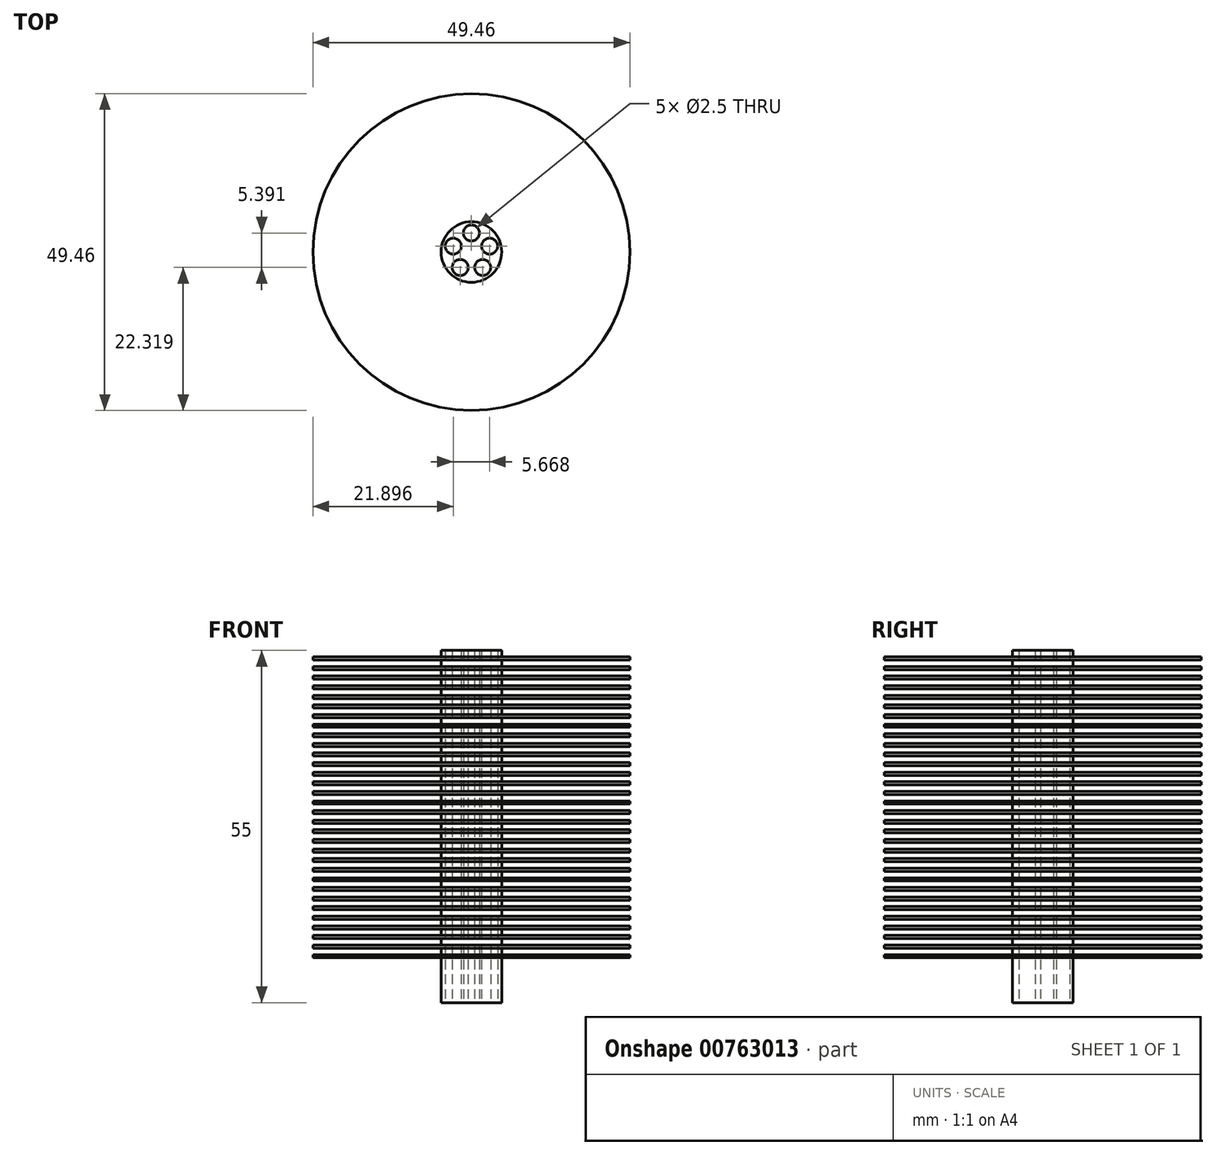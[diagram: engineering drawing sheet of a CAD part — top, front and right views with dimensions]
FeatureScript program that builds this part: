
annotation { "Feature Type Name" : "Feature", "Feature Type Description" : "" }
export const myFeature = defineFeature(function(context is Context, id is Id, definition is map)
    precondition{}
    {
        {
            var Q0;
            Q0=qCreatedBy(makeId("Top.planeOp"),FACE);
            var sketch = newSketch(context, id + "F0", { "sketchPlane" : qUnion([Q0])});
            skCircle(sketch, "E0", {"center": v(0, 0) * mm, "radius": 4.73 * mm});
            skLineSegment(sketch, "E1", {"start": v(0, 0) * mm, "end": v(0, 2.98) * mm});
            skCircle(sketch, "E2", {"center": v(0, 2.98) * mm, "radius": 1.25 * mm});
            skCircle(sketch, "E3", {"center": v(-2.83, 0.92) * mm, "radius": 1.25 * mm});
            skCircle(sketch, "E4", {"center": v(-1.75, -2.41) * mm, "radius": 1.25 * mm});
            skCircle(sketch, "E5", {"center": v(1.75, -2.41) * mm, "radius": 1.25 * mm});
            skCircle(sketch, "E6", {"center": v(2.83, 0.92) * mm, "radius": 1.25 * mm});
            skSolve(sketch);
        }
        {
            var Q0;
            Q0=makeQuery(id+"F0.imprint","IMPRINT",FACE,{"disambiguationData":[TD([[makeQuery(id+"F0.imprint","IMPRINT",EDGE,{"derivedFrom":sQuery(id+"F0.wireOp",EDGE,"E0")}),1.0]])]});
            extrude(context, id + "F1", {"entities" : qUnion([Q0]), "depth" : 50 * mm, "offsetDistance" : 25 * mm});
        }
        {
            var Q0;
            Q0=qCreatedBy(makeId("Front.planeOp"),FACE);
            var sketch = newSketch(context, id + "F2", { "sketchPlane" : qUnion([Q0])});
            skLineSegment(sketch, "E7.bottom", {"start": v(4.73, 2) * mm, "end": v(24.73, 2) * mm});
            skLineSegment(sketch, "E7.top", {"start": v(4.73, 2.5) * mm, "end": v(24.73, 2.5) * mm});
            skLineSegment(sketch, "E7.left", {"start": v(4.73, 2) * mm, "end": v(4.73, 2.5) * mm});
            skLineSegment(sketch, "E7.right", {"start": v(24.73, 2) * mm, "end": v(24.73, 2.5) * mm});
            skLineSegment(sketch, "E8.1.0.0", {"start": v(4.73, 4) * mm, "end": v(24.73, 4) * mm});
            skLineSegment(sketch, "E8.1.0.1", {"start": v(24.73, 3.5) * mm, "end": v(24.73, 4) * mm});
            skLineSegment(sketch, "E8.1.0.2", {"start": v(4.73, 3.5) * mm, "end": v(24.73, 3.5) * mm});
            skLineSegment(sketch, "E8.1.0.3", {"start": v(4.73, 3.5) * mm, "end": v(4.73, 4) * mm});
            skLineSegment(sketch, "E8.2.0.0", {"start": v(4.73, 5.5) * mm, "end": v(24.73, 5.5) * mm});
            skLineSegment(sketch, "E8.2.0.1", {"start": v(24.73, 5) * mm, "end": v(24.73, 5.5) * mm});
            skLineSegment(sketch, "E8.2.0.2", {"start": v(4.73, 5) * mm, "end": v(24.73, 5) * mm});
            skLineSegment(sketch, "E8.2.0.3", {"start": v(4.73, 5) * mm, "end": v(4.73, 5.5) * mm});
            skLineSegment(sketch, "E8.3.0.0", {"start": v(4.73, 7) * mm, "end": v(24.73, 7) * mm});
            skLineSegment(sketch, "E8.3.0.1", {"start": v(24.73, 6.5) * mm, "end": v(24.73, 7) * mm});
            skLineSegment(sketch, "E8.3.0.2", {"start": v(4.73, 6.5) * mm, "end": v(24.73, 6.5) * mm});
            skLineSegment(sketch, "E8.3.0.3", {"start": v(4.73, 6.5) * mm, "end": v(4.73, 7) * mm});
            skLineSegment(sketch, "E8.4.0.0", {"start": v(4.73, 8.5) * mm, "end": v(24.73, 8.5) * mm});
            skLineSegment(sketch, "E8.4.0.1", {"start": v(24.73, 8) * mm, "end": v(24.73, 8.5) * mm});
            skLineSegment(sketch, "E8.4.0.2", {"start": v(4.73, 8) * mm, "end": v(24.73, 8) * mm});
            skLineSegment(sketch, "E8.4.0.3", {"start": v(4.73, 8) * mm, "end": v(4.73, 8.5) * mm});
            skLineSegment(sketch, "E8.5.0.0", {"start": v(4.73, 10) * mm, "end": v(24.73, 10) * mm});
            skLineSegment(sketch, "E8.5.0.1", {"start": v(24.73, 9.5) * mm, "end": v(24.73, 10) * mm});
            skLineSegment(sketch, "E8.5.0.2", {"start": v(4.73, 9.5) * mm, "end": v(24.73, 9.5) * mm});
            skLineSegment(sketch, "E8.5.0.3", {"start": v(4.73, 9.5) * mm, "end": v(4.73, 10) * mm});
            skLineSegment(sketch, "E8.6.0.0", {"start": v(4.73, 11.5) * mm, "end": v(24.73, 11.5) * mm});
            skLineSegment(sketch, "E8.6.0.1", {"start": v(24.73, 11) * mm, "end": v(24.73, 11.5) * mm});
            skLineSegment(sketch, "E8.6.0.2", {"start": v(4.73, 11) * mm, "end": v(24.73, 11) * mm});
            skLineSegment(sketch, "E8.6.0.3", {"start": v(4.73, 11) * mm, "end": v(4.73, 11.5) * mm});
            skLineSegment(sketch, "E8.7.0.0", {"start": v(4.73, 13) * mm, "end": v(24.73, 13) * mm});
            skLineSegment(sketch, "E8.7.0.1", {"start": v(24.73, 12.5) * mm, "end": v(24.73, 13) * mm});
            skLineSegment(sketch, "E8.7.0.2", {"start": v(4.73, 12.5) * mm, "end": v(24.73, 12.5) * mm});
            skLineSegment(sketch, "E8.7.0.3", {"start": v(4.73, 12.5) * mm, "end": v(4.73, 13) * mm});
            skLineSegment(sketch, "E8.8.0.0", {"start": v(4.73, 14.5) * mm, "end": v(24.73, 14.5) * mm});
            skLineSegment(sketch, "E8.8.0.1", {"start": v(24.73, 14) * mm, "end": v(24.73, 14.5) * mm});
            skLineSegment(sketch, "E8.8.0.2", {"start": v(4.73, 14) * mm, "end": v(24.73, 14) * mm});
            skLineSegment(sketch, "E8.8.0.3", {"start": v(4.73, 14) * mm, "end": v(4.73, 14.5) * mm});
            skLineSegment(sketch, "E8.9.0.0", {"start": v(4.73, 16) * mm, "end": v(24.73, 16) * mm});
            skLineSegment(sketch, "E8.9.0.1", {"start": v(24.73, 15.5) * mm, "end": v(24.73, 16) * mm});
            skLineSegment(sketch, "E8.9.0.2", {"start": v(4.73, 15.5) * mm, "end": v(24.73, 15.5) * mm});
            skLineSegment(sketch, "E8.9.0.3", {"start": v(4.73, 15.5) * mm, "end": v(4.73, 16) * mm});
            skLineSegment(sketch, "E8.10.0.0", {"start": v(4.73, 17.5) * mm, "end": v(24.73, 17.5) * mm});
            skLineSegment(sketch, "E8.10.0.1", {"start": v(24.73, 17) * mm, "end": v(24.73, 17.5) * mm});
            skLineSegment(sketch, "E8.10.0.2", {"start": v(4.73, 17) * mm, "end": v(24.73, 17) * mm});
            skLineSegment(sketch, "E8.10.0.3", {"start": v(4.73, 17) * mm, "end": v(4.73, 17.5) * mm});
            skLineSegment(sketch, "E8.11.0.0", {"start": v(4.73, 19) * mm, "end": v(24.73, 19) * mm});
            skLineSegment(sketch, "E8.11.0.1", {"start": v(24.73, 18.5) * mm, "end": v(24.73, 19) * mm});
            skLineSegment(sketch, "E8.11.0.2", {"start": v(4.73, 18.5) * mm, "end": v(24.73, 18.5) * mm});
            skLineSegment(sketch, "E8.11.0.3", {"start": v(4.73, 18.5) * mm, "end": v(4.73, 19) * mm});
            skLineSegment(sketch, "E8.12.0.0", {"start": v(4.73, 20.5) * mm, "end": v(24.73, 20.5) * mm});
            skLineSegment(sketch, "E8.12.0.1", {"start": v(24.73, 20) * mm, "end": v(24.73, 20.5) * mm});
            skLineSegment(sketch, "E8.12.0.2", {"start": v(4.73, 20) * mm, "end": v(24.73, 20) * mm});
            skLineSegment(sketch, "E8.12.0.3", {"start": v(4.73, 20) * mm, "end": v(4.73, 20.5) * mm});
            skLineSegment(sketch, "E8.13.0.0", {"start": v(4.73, 22) * mm, "end": v(24.73, 22) * mm});
            skLineSegment(sketch, "E8.13.0.1", {"start": v(24.73, 21.5) * mm, "end": v(24.73, 22) * mm});
            skLineSegment(sketch, "E8.13.0.2", {"start": v(4.73, 21.5) * mm, "end": v(24.73, 21.5) * mm});
            skLineSegment(sketch, "E8.13.0.3", {"start": v(4.73, 21.5) * mm, "end": v(4.73, 22) * mm});
            skLineSegment(sketch, "E8.14.0.0", {"start": v(4.73, 23.5) * mm, "end": v(24.73, 23.5) * mm});
            skLineSegment(sketch, "E8.14.0.1", {"start": v(24.73, 23) * mm, "end": v(24.73, 23.5) * mm});
            skLineSegment(sketch, "E8.14.0.2", {"start": v(4.73, 23) * mm, "end": v(24.73, 23) * mm});
            skLineSegment(sketch, "E8.14.0.3", {"start": v(4.73, 23) * mm, "end": v(4.73, 23.5) * mm});
            skLineSegment(sketch, "E8.15.0.0", {"start": v(4.73, 25) * mm, "end": v(24.73, 25) * mm});
            skLineSegment(sketch, "E8.15.0.1", {"start": v(24.73, 24.5) * mm, "end": v(24.73, 25) * mm});
            skLineSegment(sketch, "E8.15.0.2", {"start": v(4.73, 24.5) * mm, "end": v(24.73, 24.5) * mm});
            skLineSegment(sketch, "E8.15.0.3", {"start": v(4.73, 24.5) * mm, "end": v(4.73, 25) * mm});
            skLineSegment(sketch, "E8.16.0.0", {"start": v(4.73, 26.5) * mm, "end": v(24.73, 26.5) * mm});
            skLineSegment(sketch, "E8.16.0.1", {"start": v(24.73, 26) * mm, "end": v(24.73, 26.5) * mm});
            skLineSegment(sketch, "E8.16.0.2", {"start": v(4.73, 26) * mm, "end": v(24.73, 26) * mm});
            skLineSegment(sketch, "E8.16.0.3", {"start": v(4.73, 26) * mm, "end": v(4.73, 26.5) * mm});
            skLineSegment(sketch, "E8.17.0.0", {"start": v(4.73, 28) * mm, "end": v(24.73, 28) * mm});
            skLineSegment(sketch, "E8.17.0.1", {"start": v(24.73, 27.5) * mm, "end": v(24.73, 28) * mm});
            skLineSegment(sketch, "E8.17.0.2", {"start": v(4.73, 27.5) * mm, "end": v(24.73, 27.5) * mm});
            skLineSegment(sketch, "E8.17.0.3", {"start": v(4.73, 27.5) * mm, "end": v(4.73, 28) * mm});
            skLineSegment(sketch, "E8.18.0.0", {"start": v(4.73, 29.5) * mm, "end": v(24.73, 29.5) * mm});
            skLineSegment(sketch, "E8.18.0.1", {"start": v(24.73, 29) * mm, "end": v(24.73, 29.5) * mm});
            skLineSegment(sketch, "E8.18.0.2", {"start": v(4.73, 29) * mm, "end": v(24.73, 29) * mm});
            skLineSegment(sketch, "E8.18.0.3", {"start": v(4.73, 29) * mm, "end": v(4.73, 29.5) * mm});
            skLineSegment(sketch, "E8.19.0.0", {"start": v(4.73, 31) * mm, "end": v(24.73, 31) * mm});
            skLineSegment(sketch, "E8.19.0.1", {"start": v(24.73, 30.5) * mm, "end": v(24.73, 31) * mm});
            skLineSegment(sketch, "E8.19.0.2", {"start": v(4.73, 30.5) * mm, "end": v(24.73, 30.5) * mm});
            skLineSegment(sketch, "E8.19.0.3", {"start": v(4.73, 30.5) * mm, "end": v(4.73, 31) * mm});
            skLineSegment(sketch, "E8.20.0.0", {"start": v(4.73, 32.5) * mm, "end": v(24.73, 32.5) * mm});
            skLineSegment(sketch, "E8.20.0.1", {"start": v(24.73, 32) * mm, "end": v(24.73, 32.5) * mm});
            skLineSegment(sketch, "E8.20.0.2", {"start": v(4.73, 32) * mm, "end": v(24.73, 32) * mm});
            skLineSegment(sketch, "E8.20.0.3", {"start": v(4.73, 32) * mm, "end": v(4.73, 32.5) * mm});
            skLineSegment(sketch, "E8.21.0.0", {"start": v(4.73, 34) * mm, "end": v(24.73, 34) * mm});
            skLineSegment(sketch, "E8.21.0.1", {"start": v(24.73, 33.5) * mm, "end": v(24.73, 34) * mm});
            skLineSegment(sketch, "E8.21.0.2", {"start": v(4.73, 33.5) * mm, "end": v(24.73, 33.5) * mm});
            skLineSegment(sketch, "E8.21.0.3", {"start": v(4.73, 33.5) * mm, "end": v(4.73, 34) * mm});
            skLineSegment(sketch, "E8.22.0.0", {"start": v(4.73, 35.5) * mm, "end": v(24.73, 35.5) * mm});
            skLineSegment(sketch, "E8.22.0.1", {"start": v(24.73, 35) * mm, "end": v(24.73, 35.5) * mm});
            skLineSegment(sketch, "E8.22.0.2", {"start": v(4.73, 35) * mm, "end": v(24.73, 35) * mm});
            skLineSegment(sketch, "E8.22.0.3", {"start": v(4.73, 35) * mm, "end": v(4.73, 35.5) * mm});
            skLineSegment(sketch, "E8.23.0.0", {"start": v(4.73, 37) * mm, "end": v(24.73, 37) * mm});
            skLineSegment(sketch, "E8.23.0.1", {"start": v(24.73, 36.5) * mm, "end": v(24.73, 37) * mm});
            skLineSegment(sketch, "E8.23.0.2", {"start": v(4.73, 36.5) * mm, "end": v(24.73, 36.5) * mm});
            skLineSegment(sketch, "E8.23.0.3", {"start": v(4.73, 36.5) * mm, "end": v(4.73, 37) * mm});
            skLineSegment(sketch, "E8.24.0.0", {"start": v(4.73, 38.5) * mm, "end": v(24.73, 38.5) * mm});
            skLineSegment(sketch, "E8.24.0.1", {"start": v(24.73, 38) * mm, "end": v(24.73, 38.5) * mm});
            skLineSegment(sketch, "E8.24.0.2", {"start": v(4.73, 38) * mm, "end": v(24.73, 38) * mm});
            skLineSegment(sketch, "E8.24.0.3", {"start": v(4.73, 38) * mm, "end": v(4.73, 38.5) * mm});
            skLineSegment(sketch, "E8.25.0.0", {"start": v(4.73, 40) * mm, "end": v(24.73, 40) * mm});
            skLineSegment(sketch, "E8.25.0.1", {"start": v(24.73, 39.5) * mm, "end": v(24.73, 40) * mm});
            skLineSegment(sketch, "E8.25.0.2", {"start": v(4.73, 39.5) * mm, "end": v(24.73, 39.5) * mm});
            skLineSegment(sketch, "E8.25.0.3", {"start": v(4.73, 39.5) * mm, "end": v(4.73, 40) * mm});
            skLineSegment(sketch, "E8.26.0.0", {"start": v(4.73, 41.5) * mm, "end": v(24.73, 41.5) * mm});
            skLineSegment(sketch, "E8.26.0.1", {"start": v(24.73, 41) * mm, "end": v(24.73, 41.5) * mm});
            skLineSegment(sketch, "E8.26.0.2", {"start": v(4.73, 41) * mm, "end": v(24.73, 41) * mm});
            skLineSegment(sketch, "E8.26.0.3", {"start": v(4.73, 41) * mm, "end": v(4.73, 41.5) * mm});
            skLineSegment(sketch, "E8.27.0.0", {"start": v(4.73, 43) * mm, "end": v(24.73, 43) * mm});
            skLineSegment(sketch, "E8.27.0.1", {"start": v(24.73, 42.5) * mm, "end": v(24.73, 43) * mm});
            skLineSegment(sketch, "E8.27.0.2", {"start": v(4.73, 42.5) * mm, "end": v(24.73, 42.5) * mm});
            skLineSegment(sketch, "E8.27.0.3", {"start": v(4.73, 42.5) * mm, "end": v(4.73, 43) * mm});
            skLineSegment(sketch, "E8.28.0.0", {"start": v(4.73, 44.5) * mm, "end": v(24.73, 44.5) * mm});
            skLineSegment(sketch, "E8.28.0.1", {"start": v(24.73, 44) * mm, "end": v(24.73, 44.5) * mm});
            skLineSegment(sketch, "E8.28.0.2", {"start": v(4.73, 44) * mm, "end": v(24.73, 44) * mm});
            skLineSegment(sketch, "E8.28.0.3", {"start": v(4.73, 44) * mm, "end": v(4.73, 44.5) * mm});
            skLineSegment(sketch, "E8.29.0.0", {"start": v(4.73, 46) * mm, "end": v(24.73, 46) * mm});
            skLineSegment(sketch, "E8.29.0.1", {"start": v(24.73, 45.5) * mm, "end": v(24.73, 46) * mm});
            skLineSegment(sketch, "E8.29.0.2", {"start": v(4.73, 45.5) * mm, "end": v(24.73, 45.5) * mm});
            skLineSegment(sketch, "E8.29.0.3", {"start": v(4.73, 45.5) * mm, "end": v(4.73, 46) * mm});
            skLineSegment(sketch, "E8.direction1", {"start": v(4.73, 2) * mm, "end": v(4.73, 3.5) * mm, "construction": true});
            skLineSegment(sketch, "E9", {"start": v(0, 0) * mm, "end": v(0, 60.8) * mm});
            skLineSegment(sketch, "E10.0.30.0", {"start": v(4.73, 47.5) * mm, "end": v(24.73, 47.5) * mm});
            skLineSegment(sketch, "E10.3.30.0", {"start": v(24.73, 47) * mm, "end": v(24.73, 47.5) * mm});
            skLineSegment(sketch, "E10.6.30.0", {"start": v(4.73, 47) * mm, "end": v(24.73, 47) * mm});
            skLineSegment(sketch, "E10.9.30.0", {"start": v(4.73, 47) * mm, "end": v(4.73, 47.5) * mm});
            skLineSegment(sketch, "E10.0.31.0", {"start": v(4.73, 49) * mm, "end": v(24.73, 49) * mm});
            skLineSegment(sketch, "E10.3.31.0", {"start": v(24.73, 48.5) * mm, "end": v(24.73, 49) * mm});
            skLineSegment(sketch, "E10.6.31.0", {"start": v(4.73, 48.5) * mm, "end": v(24.73, 48.5) * mm});
            skLineSegment(sketch, "E10.9.31.0", {"start": v(4.73, 48.5) * mm, "end": v(4.73, 49) * mm});
            skSolve(sketch);
        }
        {
            var Q0;
            Q0=makeQuery(id+"F2.imprint","IMPRINT",FACE,{"disambiguationData":[TD([[makeQuery(id+"F2.imprint","IMPRINT",EDGE,{"derivedFrom":sQuery(id+"F2.wireOp",EDGE,"E7.bottom")}),1.0]])]});
            var Q1;
            Q1=makeQuery(id+"F2.imprint","IMPRINT",FACE,{"disambiguationData":[TD([[makeQuery(id+"F2.imprint","IMPRINT",EDGE,{"derivedFrom":sQuery(id+"F2.wireOp",EDGE,"E8.1.0.0")}),-1.0]])]});
            var Q2;
            Q2=makeQuery(id+"F2.imprint","IMPRINT",FACE,{"disambiguationData":[TD([[makeQuery(id+"F2.imprint","IMPRINT",EDGE,{"derivedFrom":sQuery(id+"F2.wireOp",EDGE,"E8.2.0.0")}),-1.0]])]});
            var Q3;
            Q3=makeQuery(id+"F2.imprint","IMPRINT",FACE,{"disambiguationData":[TD([[makeQuery(id+"F2.imprint","IMPRINT",EDGE,{"derivedFrom":sQuery(id+"F2.wireOp",EDGE,"E8.3.0.0")}),-1.0]])]});
            var Q4;
            Q4=makeQuery(id+"F2.imprint","IMPRINT",FACE,{"disambiguationData":[TD([[makeQuery(id+"F2.imprint","IMPRINT",EDGE,{"derivedFrom":sQuery(id+"F2.wireOp",EDGE,"E8.4.0.0")}),-1.0]])]});
            var Q5;
            Q5=makeQuery(id+"F2.imprint","IMPRINT",FACE,{"disambiguationData":[TD([[makeQuery(id+"F2.imprint","IMPRINT",EDGE,{"derivedFrom":sQuery(id+"F2.wireOp",EDGE,"E8.5.0.0")}),-1.0]])]});
            var Q6;
            Q6=makeQuery(id+"F2.imprint","IMPRINT",FACE,{"disambiguationData":[TD([[makeQuery(id+"F2.imprint","IMPRINT",EDGE,{"derivedFrom":sQuery(id+"F2.wireOp",EDGE,"E8.6.0.0")}),-1.0]])]});
            var Q7;
            Q7=makeQuery(id+"F2.imprint","IMPRINT",FACE,{"disambiguationData":[TD([[makeQuery(id+"F2.imprint","IMPRINT",EDGE,{"derivedFrom":sQuery(id+"F2.wireOp",EDGE,"E8.7.0.0")}),-1.0]])]});
            var Q8;
            Q8=makeQuery(id+"F2.imprint","IMPRINT",FACE,{"disambiguationData":[TD([[makeQuery(id+"F2.imprint","IMPRINT",EDGE,{"derivedFrom":sQuery(id+"F2.wireOp",EDGE,"E8.8.0.0")}),-1.0]])]});
            var Q9;
            Q9=makeQuery(id+"F2.imprint","IMPRINT",FACE,{"disambiguationData":[TD([[makeQuery(id+"F2.imprint","IMPRINT",EDGE,{"derivedFrom":sQuery(id+"F2.wireOp",EDGE,"E8.9.0.0")}),-1.0]])]});
            var Q10;
            Q10=makeQuery(id+"F2.imprint","IMPRINT",FACE,{"disambiguationData":[TD([[makeQuery(id+"F2.imprint","IMPRINT",EDGE,{"derivedFrom":sQuery(id+"F2.wireOp",EDGE,"E8.10.0.0")}),-1.0]])]});
            var Q11;
            Q11=makeQuery(id+"F2.imprint","IMPRINT",FACE,{"disambiguationData":[TD([[makeQuery(id+"F2.imprint","IMPRINT",EDGE,{"derivedFrom":sQuery(id+"F2.wireOp",EDGE,"E8.11.0.0")}),-1.0]])]});
            var Q12;
            Q12=makeQuery(id+"F2.imprint","IMPRINT",FACE,{"disambiguationData":[TD([[makeQuery(id+"F2.imprint","IMPRINT",EDGE,{"derivedFrom":sQuery(id+"F2.wireOp",EDGE,"E8.23.0.0")}),-1.0]])]});
            var Q13;
            Q13=makeQuery(id+"F2.imprint","IMPRINT",FACE,{"disambiguationData":[TD([[makeQuery(id+"F2.imprint","IMPRINT",EDGE,{"derivedFrom":sQuery(id+"F2.wireOp",EDGE,"E8.24.0.0")}),-1.0]])]});
            var Q14;
            Q14=makeQuery(id+"F2.imprint","IMPRINT",FACE,{"disambiguationData":[TD([[makeQuery(id+"F2.imprint","IMPRINT",EDGE,{"derivedFrom":sQuery(id+"F2.wireOp",EDGE,"E8.25.0.0")}),-1.0]])]});
            var Q15;
            Q15=makeQuery(id+"F2.imprint","IMPRINT",FACE,{"disambiguationData":[TD([[makeQuery(id+"F2.imprint","IMPRINT",EDGE,{"derivedFrom":sQuery(id+"F2.wireOp",EDGE,"E8.26.0.0")}),-1.0]])]});
            var Q16;
            Q16=makeQuery(id+"F2.imprint","IMPRINT",FACE,{"disambiguationData":[TD([[makeQuery(id+"F2.imprint","IMPRINT",EDGE,{"derivedFrom":sQuery(id+"F2.wireOp",EDGE,"E8.27.0.0")}),-1.0]])]});
            var Q17;
            Q17=makeQuery(id+"F2.imprint","IMPRINT",FACE,{"disambiguationData":[TD([[makeQuery(id+"F2.imprint","IMPRINT",EDGE,{"derivedFrom":sQuery(id+"F2.wireOp",EDGE,"E8.28.0.0")}),-1.0]])]});
            var Q18;
            Q18=makeQuery(id+"F2.imprint","IMPRINT",FACE,{"disambiguationData":[TD([[makeQuery(id+"F2.imprint","IMPRINT",EDGE,{"derivedFrom":sQuery(id+"F2.wireOp",EDGE,"E8.16.0.0")}),-1.0]])]});
            var Q19;
            Q19=makeQuery(id+"F2.imprint","IMPRINT",FACE,{"disambiguationData":[TD([[makeQuery(id+"F2.imprint","IMPRINT",EDGE,{"derivedFrom":sQuery(id+"F2.wireOp",EDGE,"E8.17.0.0")}),-1.0]])]});
            var Q20;
            Q20=makeQuery(id+"F2.imprint","IMPRINT",FACE,{"disambiguationData":[TD([[makeQuery(id+"F2.imprint","IMPRINT",EDGE,{"derivedFrom":sQuery(id+"F2.wireOp",EDGE,"E8.18.0.0")}),-1.0]])]});
            var Q21;
            Q21=makeQuery(id+"F2.imprint","IMPRINT",FACE,{"disambiguationData":[TD([[makeQuery(id+"F2.imprint","IMPRINT",EDGE,{"derivedFrom":sQuery(id+"F2.wireOp",EDGE,"E8.13.0.0")}),-1.0]])]});
            var Q22;
            Q22=makeQuery(id+"F2.imprint","IMPRINT",FACE,{"disambiguationData":[TD([[makeQuery(id+"F2.imprint","IMPRINT",EDGE,{"derivedFrom":sQuery(id+"F2.wireOp",EDGE,"E8.14.0.0")}),-1.0]])]});
            var Q23;
            Q23=makeQuery(id+"F2.imprint","IMPRINT",FACE,{"disambiguationData":[TD([[makeQuery(id+"F2.imprint","IMPRINT",EDGE,{"derivedFrom":sQuery(id+"F2.wireOp",EDGE,"E8.12.0.0")}),-1.0]])]});
            var Q24;
            Q24=makeQuery(id+"F2.imprint","IMPRINT",FACE,{"disambiguationData":[TD([[makeQuery(id+"F2.imprint","IMPRINT",EDGE,{"derivedFrom":sQuery(id+"F2.wireOp",EDGE,"E8.19.0.0")}),-1.0]])]});
            var Q25;
            Q25=makeQuery(id+"F2.imprint","IMPRINT",FACE,{"disambiguationData":[TD([[makeQuery(id+"F2.imprint","IMPRINT",EDGE,{"derivedFrom":sQuery(id+"F2.wireOp",EDGE,"E8.20.0.0")}),-1.0]])]});
            var Q26;
            Q26=makeQuery(id+"F2.imprint","IMPRINT",FACE,{"disambiguationData":[TD([[makeQuery(id+"F2.imprint","IMPRINT",EDGE,{"derivedFrom":sQuery(id+"F2.wireOp",EDGE,"E8.21.0.0")}),-1.0]])]});
            var Q27;
            Q27=makeQuery(id+"F2.imprint","IMPRINT",FACE,{"disambiguationData":[TD([[makeQuery(id+"F2.imprint","IMPRINT",EDGE,{"derivedFrom":sQuery(id+"F2.wireOp",EDGE,"E8.22.0.0")}),-1.0]])]});
            var Q28;
            Q28=makeQuery(id+"F2.imprint","IMPRINT",FACE,{"disambiguationData":[TD([[makeQuery(id+"F2.imprint","IMPRINT",EDGE,{"derivedFrom":sQuery(id+"F2.wireOp",EDGE,"E8.29.0.0")}),-1.0]])]});
            var Q29;
            Q29=makeQuery(id+"F2.imprint","IMPRINT",FACE,{"disambiguationData":[TD([[makeQuery(id+"F2.imprint","IMPRINT",EDGE,{"derivedFrom":sQuery(id+"F2.wireOp",EDGE,"E8.15.0.0")}),-1.0]])]});
            var Q30;
            Q30=sQuery(id+"F2.wireOp",EDGE,"E9");
            revolve(context, id + "F3", {"operationType" : NewBodyOperationType.ADD, "surfaceOperationType" : NewSurfaceOperationType.NEW, "entities" : qUnion([Q0, Q1, Q2, Q3, Q4, Q5, Q6, Q7, Q8, Q9, Q10, Q11, Q12, Q13, Q14, Q15, Q16, Q17, Q18, Q19, Q20, Q21, Q22, Q23, Q24, Q25, Q26, Q27, Q28, Q29]), "axis" : qUnion([Q30]), "revolveType" : RevolveType.FULL});
        }
        {
            var Q0;
            Q0=makeQuery(id+"F2.imprint","IMPRINT",FACE,{"disambiguationData":[TD([[makeQuery(id+"F2.imprint","IMPRINT",EDGE,{"derivedFrom":sQuery(id+"F2.wireOp",EDGE,"E10.0.31.0")}),-1.0]])]});
            var Q1;
            Q1=makeQuery(id+"F2.imprint","IMPRINT",FACE,{"disambiguationData":[TD([[makeQuery(id+"F2.imprint","IMPRINT",EDGE,{"derivedFrom":sQuery(id+"F2.wireOp",EDGE,"E10.0.30.0")}),-1.0]])]});
            var Q2;
            Q2=sQuery(id+"F2.wireOp",EDGE,"E9");
            revolve(context, id + "F4", {"operationType" : NewBodyOperationType.ADD, "surfaceOperationType" : NewSurfaceOperationType.NEW, "entities" : qUnion([Q0, Q1]), "axis" : qUnion([Q2]), "revolveType" : RevolveType.FULL});
        }
        {
            var Q0;
            Q0=makeQuery(id+"F1.opExtrude","CAP_FACE",FACE,{"disambiguationData":[OSD([sQuery(id+"F0.wireOp",EDGE,"E0"),sQuery(id+"F0.wireOp",EDGE,"E2"),sQuery(id+"F0.wireOp",EDGE,"E3"),sQuery(id+"F0.wireOp",EDGE,"E4"),sQuery(id+"F0.wireOp",EDGE,"E5"),sQuery(id+"F0.wireOp",EDGE,"E6")])],"isStart":true});
            extrude(context, id + "F5", {"entities" : qUnion([Q0]), "operationType" : NewBodyOperationType.ADD, "depth" : 5 * mm, "offsetDistance" : 25 * mm});
        }
    });
